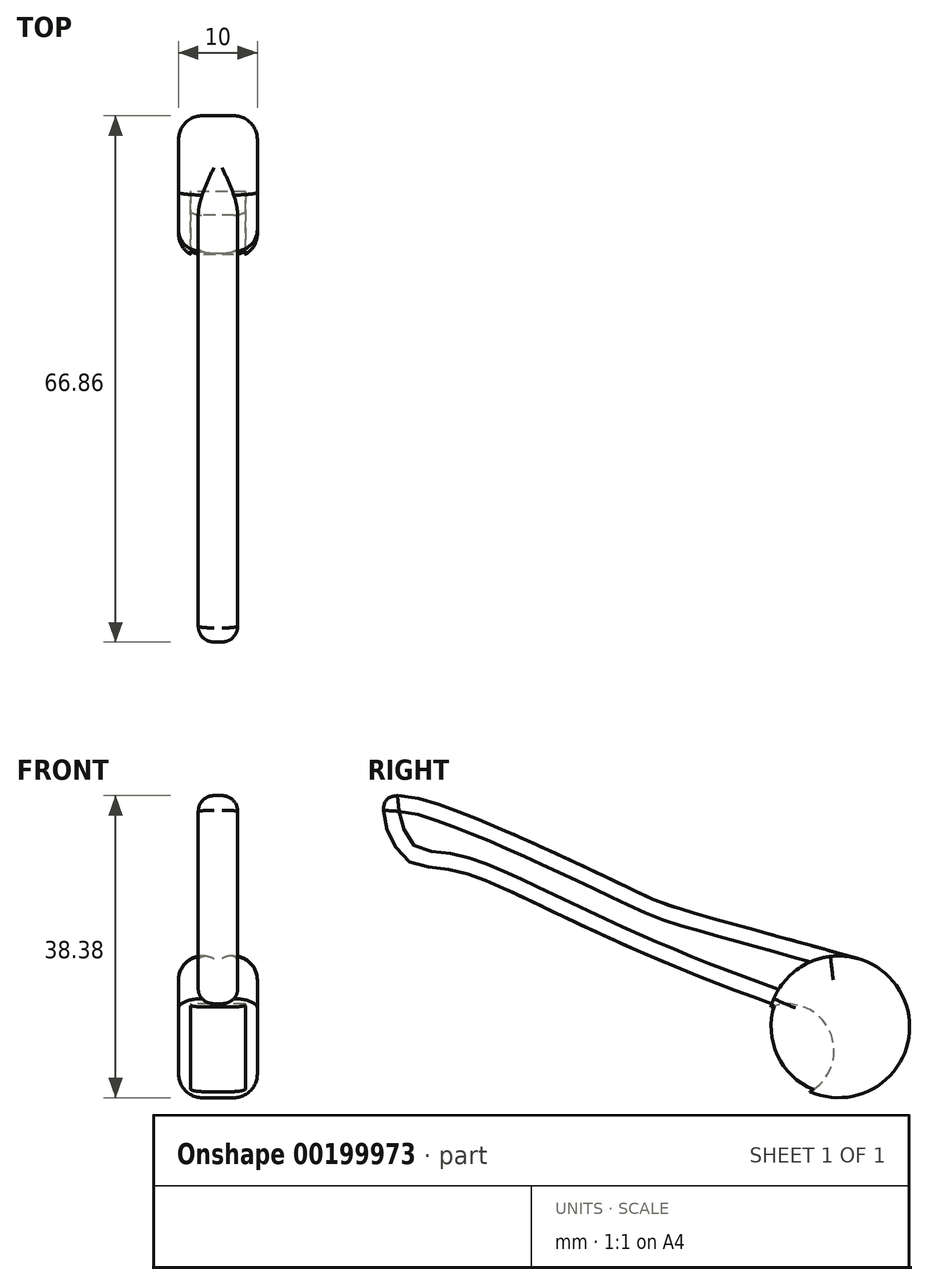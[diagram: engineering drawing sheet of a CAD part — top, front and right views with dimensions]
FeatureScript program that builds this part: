
annotation { "Feature Type Name" : "Feature", "Feature Type Description" : "" }
export const myFeature = defineFeature(function(context is Context, id is Id, definition is map)
    precondition{}
    {
        {
            var Q0;
            Q0=qCreatedBy(makeId("Right.planeOp"),FACE);
            var sketch = newSketch(context, id + "F0", { "sketchPlane" : qUnion([Q0])});
            skCircle(sketch, "E0", {"center": v(31.65, 0) * mm, "radius": 9 * mm});
            skFitSpline(sketch, "E1", {"points": [v(34.07, 8.67) * mm, v(4.9, 17.69) * mm, v(-20.34, 28.6) * mm, v(-26.08, 28.33) * mm, v(-23.53, 21.45) * mm, v(-17.54, 19.96) * mm, v(23.14, 2.94) * mm], "startDerivative": vector(-340.39, 95.03) * mm, "endDerivative": vector(264.2, -93.53) * mm});
            skSolve(sketch);
        }
        {
            var Q0;
            {var subQ0=sQuery(id+"F0.wireOp",EDGE,"E1");var subQ1=sQuery(id+"F0.wireOp",EDGE,"E0");var subQ2=makeQuery(id+"F0.imprint","INTERSECT",VERTEX,{"disambiguationData":[OD(0.0)],"derivedFrom":[subQ1,subQ0]});Q0=makeQuery(id+"F0.imprint","IMPRINT",FACE,{"disambiguationData":[TD([[makeQuery(id+"F0.imprint","IMPRINT",EDGE,{"disambiguationData":[TD([[subQ2,-1.0]])],"derivedFrom":subQ1}),-1.0]])]});}
            extrude(context, id + "F1", {"entities" : qUnion([Q0]), "endBound" : BoundingType.SYMMETRIC, "depth" : 5 * mm});
        }
        {
            var Q0;
            {var subQ0=sQuery(id+"F0.wireOp",EDGE,"E1");var subQ1=sQuery(id+"F0.wireOp",EDGE,"E0");var subQ2=makeQuery(id+"F0.imprint","INTERSECT",VERTEX,{"disambiguationData":[OD(0.0)],"derivedFrom":[subQ1,subQ0]});Q0=makeQuery(id+"F0.imprint","IMPRINT",FACE,{"disambiguationData":[TD([[makeQuery(id+"F0.imprint","IMPRINT",EDGE,{"disambiguationData":[TD([[subQ2,-1.0]])],"derivedFrom":subQ1}),1.0]])]});}
            extrude(context, id + "F2", {"entities" : qUnion([Q0]), "operationType" : NewBodyOperationType.ADD, "endBound" : BoundingType.SYMMETRIC, "depth" : 10 * mm});
        }
        {
            var Q0;
            Q0=makeQuery(id+"F1.opExtrude","CAP_EDGE",EDGE,{"disambiguationData":[OSD([sQuery(id+"F0.wireOp",EDGE,"E1")])],"isStart":true});
            var Q1;
            Q1=makeQuery(id+"F1.opExtrude","CAP_EDGE",EDGE,{"disambiguationData":[OSD([sQuery(id+"F0.wireOp",EDGE,"E1")])],"isStart":false});
            fillet(context, id + "F3", {"entities" : qUnion([Q0, Q1]), "radius" : 2 * mm, "tangentPropagation" : true, "allowEdgeOverflow" : false});
        }
        {
            var Q0;
            Q0=qCreatedBy(makeId("Right.planeOp"),FACE);
            var sketch = newSketch(context, id + "F4", { "sketchPlane" : qUnion([Q0])});
            skCircle(sketch, "E2", {"center": v(25.1, -3.05) * mm, "radius": 5.95 * mm});
            skCircle(sketch, "E3.0", {"center": v(31.65, 0) * mm, "radius": 9 * mm, "construction": true});
            skLineSegment(sketch, "E4", {"start": v(0, -9) * mm, "end": v(73.47, -9) * mm, "construction": true});
            skSolve(sketch);
        }
        {
            var Q0;
            Q0=makeQuery(id+"F4.imprint","IMPRINT",FACE,{"disambiguationData":[TD([[makeQuery(id+"F4.imprint","IMPRINT",EDGE,{"derivedFrom":sQuery(id+"F4.wireOp",EDGE,"E2")}),1.0]])]});
            var Q1;
            Q1=sQuery(id+"F4.wireOp",EDGE,"E2");
            extrude(context, id + "F5", {"entities" : qUnion([Q0]), "operationType" : NewBodyOperationType.REMOVE, "surfaceEntities" : qUnion([Q1]), "endBound" : BoundingType.SYMMETRIC, "depth" : 7 * mm});
        }
        {
            var Q0;
            Q0=makeQuery(id+"F2.opExtrude","CAP_EDGE",EDGE,{"disambiguationData":[OSD([sQuery(id+"F0.wireOp",EDGE,"E0")])],"isStart":true});
            var Q1;
            Q1=makeQuery(id+"F2.opExtrude","CAP_EDGE",EDGE,{"disambiguationData":[OSD([sQuery(id+"F0.wireOp",EDGE,"E0")])],"isStart":false});
            fillet(context, id + "F6", {"entities" : qUnion([Q0, Q1]), "radius" : 3 * mm, "tangentPropagation" : true, "allowEdgeOverflow" : false});
        }
    });
